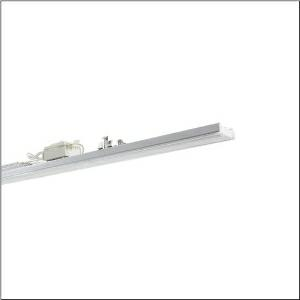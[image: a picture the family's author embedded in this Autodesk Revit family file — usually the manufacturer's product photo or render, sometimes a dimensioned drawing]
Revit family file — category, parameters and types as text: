
# Revit family: licross_21_recessed_ho_52tl12dn3exm
name_source: partatom
category: Lighting Fixtures
units: mm (PartAtom-declared; Revit-internal decimal feet)

## family parameters
Cut with Voids When Loaded = No
Host = Face
Light Source = No
Part Type = Normal
Room Calculation Point = No
Round Connector Dimension = Use Diameter
Shared = No

## types (1)
- --- (1 x LED, 14040 lm, 84.6 W, 3000K)
    Apparent Load = 85 VA
    CIE Flux Codes = 69 91 98 100 100
    Color Rendering = 80
    Color Temperature = 3000K
    Default Elevation = 1800 mm
    Description = Licross 21 Recessed HO, luminaire insert, of sheet steel, galvanised, coil coated, white, length: 1.500mm, width: 66mm, height: 67mm, LED rated luminous flux: 14.040lm, light colour: 830, SDCM (Standard Deviation of Colour Matching)MacAdam ≤ 3 SDCM (initial), control gear: DALI 2, with plug, 5-pole, with phase selection, mains connection: 220..240V, AC, 50/60Hz, rated input power: 85W, internal wiring halogen-free, primary optical cover: cover, of PMMA, light emission: direct distribution, primary light characteristic: symmetric, protection rating (complete): IP40, insulation class (complete): insulation class I (protective earthing), certification: CE, ENEC, VDE, UKCA, protection symbol: D if used in an environment without relevant dust loads with corresponding accessories, impact resistance: IK06, permissible ambient temperature for indoor applications: -25..+30°C, corresponds to IFS (International Featured Standards) requirements for safety and quality in the food industry, reducing of maximum allowable ambient temperature of 5°C with ceiling mounting, LABS conformity tested according to VDMA 24364:2018-05, The light source and the operating device comply with the requirements of the Ecodesign Regulation (EU) 2019/2020 and are replaceable in accordance with this regulation, packaging unit: 1 piece
    Height = 58 mm
    Lamp = 1 x LED
    Lamp Light Flux = 14040 lm
    Lamp Power = 84.6 W
    Lamp count = 1
    Length = 1500 mm
    Luminous efficacy = 166 lm/W
    Manufacturer = Siteco
    ModVariant = No
    Model = 52TL12DN3EXM
    Mounting Place = Ceiling
    Mounting Type = Pendant
    Number of Poles = 1
    OnlyDefault = Yes
    Power Factor = 1
    Product Name = Licross 21 Recessed HO
    Product group = luminaire insert | ceiling pendant
    ProductGroupID = 901
    Protection Class = Protection class I
    Protection Degree = IP 40
    RLX_Detail_Level = 1
    RLX_Emergency_Light_Flux = 0 lm
    RLX_Emergency_Type = 0
    RLX_Emergency_Type_DB = No
    RlxData = <blob elided: 25001 chars, md5=1bd8ed8c>
    Socket = socket
    Standby Power = 0 W
    System Light Flux = 14040 lm
    System Power = 85 W
    Type Comments = factory setting: luminous flux: 100 % | dim-lin: 254 | 484 mA
    Type Image = l_1296930.jpg
    URL = http://relux.com
    VarID = @adj_092951
    Voltage = 0 V
    Weight = 0.00 kg
    Width = 66 mm

## geometry (parser evidence)
native form markers: Blend x4, Sweep x12
no freeform markers — native parametric forms only
